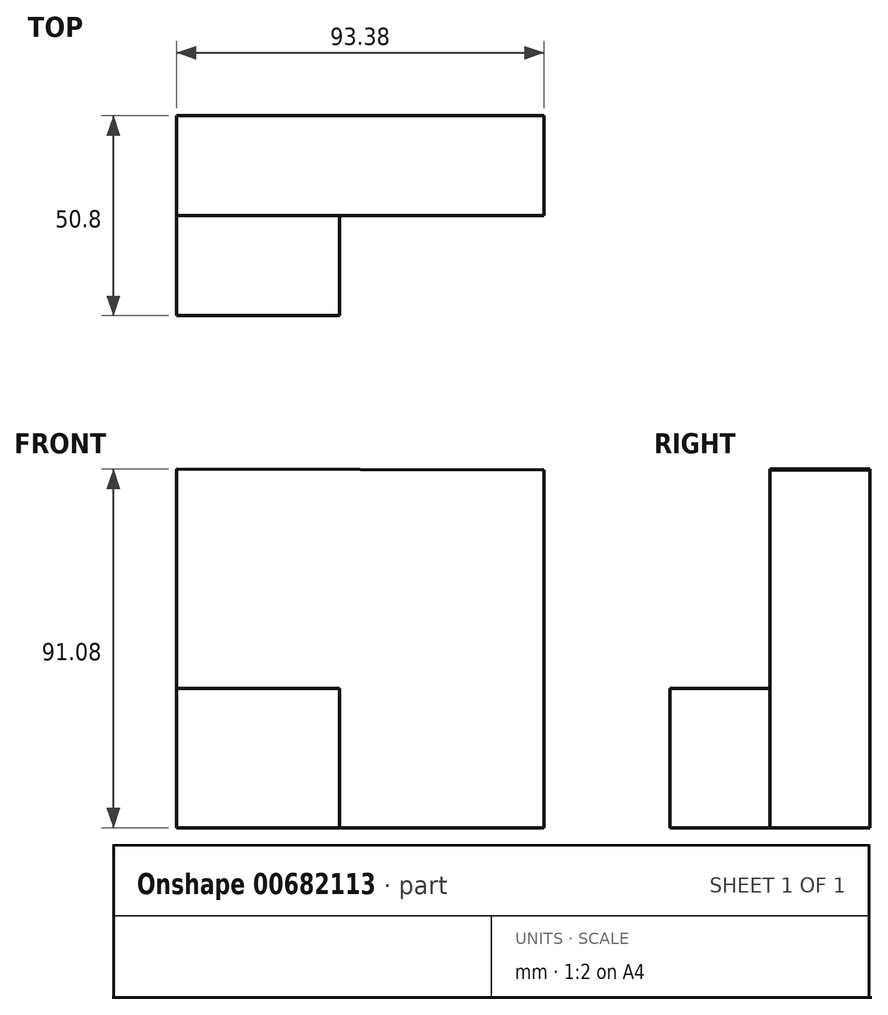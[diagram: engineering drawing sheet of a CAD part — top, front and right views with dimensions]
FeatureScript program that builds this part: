
annotation { "Feature Type Name" : "Feature", "Feature Type Description" : "" }
export const myFeature = defineFeature(function(context is Context, id is Id, definition is map)
    precondition{}
    {
        {
            var Q0;
            Q0=qCreatedBy(makeId("Front.planeOp"),FACE);
            var sketch = newSketch(context, id + "F0", { "sketchPlane" : qUnion([Q0])});
            skLineSegment(sketch, "E0", {"start": v(-54.7, 55.66) * mm, "end": v(-54.7, -35.42) * mm});
            skLineSegment(sketch, "E1", {"start": v(-54.7, -35.42) * mm, "end": v(38.67, -35.42) * mm});
            skLineSegment(sketch, "E2", {"start": v(38.67, -35.42) * mm, "end": v(38.67, 55.47) * mm});
            skLineSegment(sketch, "E3", {"start": v(38.67, 55.47) * mm, "end": v(-54.7, 55.66) * mm});
            skSolve(sketch);
        }
        {
            var Q0;
            Q0 = qSketchRegion(id + "F0", true);
            extrude(context, id + "F1", {"entities" : qUnion([Q0]), "depth" : 25.4 * mm, "offsetDistance" : 25.4 * mm});
        }
        {
            var Q0;
            Q0=makeQuery(id+"F1.opExtrude","CAP_FACE",FACE,{"disambiguationData":[OSD([sQuery(id+"F0.wireOp",EDGE,"E0"),sQuery(id+"F0.wireOp",EDGE,"E1"),sQuery(id+"F0.wireOp",EDGE,"E2"),sQuery(id+"F0.wireOp",EDGE,"E3")])],"isStart":false});
            var sketch = newSketch(context, id + "F2", { "sketchPlane" : qUnion([Q0])});
            skLineSegment(sketch, "E4.bottom", {"start": v(-54.7, -35.42) * mm, "end": v(-13.27, -35.42) * mm});
            skLineSegment(sketch, "E4.top", {"start": v(-54.7, 0) * mm, "end": v(-13.27, 0) * mm});
            skLineSegment(sketch, "E4.left", {"start": v(-54.7, -35.42) * mm, "end": v(-54.7, 0) * mm});
            skLineSegment(sketch, "E4.right", {"start": v(-13.27, -35.42) * mm, "end": v(-13.27, 0) * mm});
            skSolve(sketch);
        }
        {
            var Q0;
            Q0 = qSketchRegion(id + "F2", true);
            extrude(context, id + "F3", {"entities" : qUnion([Q0]), "operationType" : NewBodyOperationType.ADD, "depth" : 25.4 * mm, "offsetDistance" : 25.4 * mm});
        }
    });
